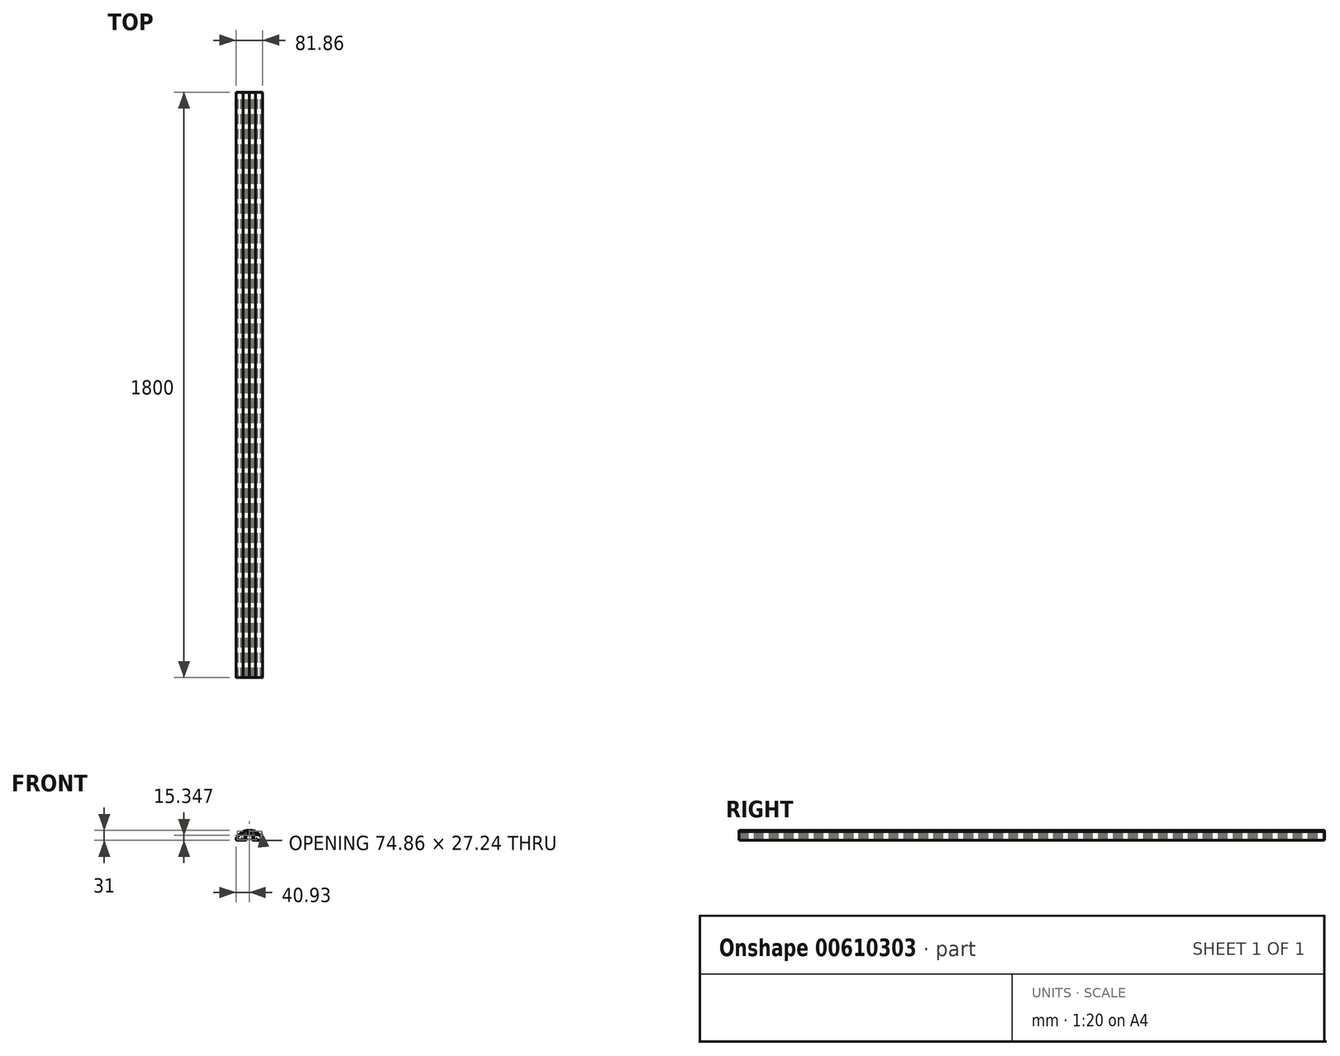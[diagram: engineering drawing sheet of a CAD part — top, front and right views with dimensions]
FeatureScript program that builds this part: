
annotation { "Feature Type Name" : "Feature", "Feature Type Description" : "" }
export const myFeature = defineFeature(function(context is Context, id is Id, definition is map)
    precondition{}
    {
        {
            var Q0;
            Q0=qCreatedBy(makeId("Front.planeOp"),FACE);
            var sketch = newSketch(context, id + "F0", { "sketchPlane" : qUnion([Q0])});
            skLineSegment(sketch, "E0.bottom", {"start": v(-41, 15.63) * mm, "end": v(41, 15.63) * mm, "construction": true});
            skLineSegment(sketch, "E0.top", {"start": v(-41, -15.37) * mm, "end": v(41, -15.37) * mm, "construction": true});
            skLineSegment(sketch, "E0.left", {"start": v(-41, 15.63) * mm, "end": v(-41, -15.37) * mm, "construction": true});
            skLineSegment(sketch, "E0.right", {"start": v(41, 15.63) * mm, "end": v(41, -15.37) * mm, "construction": true});
            skLineSegment(sketch, "E1", {"start": v(0, 15.63) * mm, "end": v(0, -15.37) * mm, "construction": true});
            skLineSegment(sketch, "E2", {"start": v(-41, 0.13) * mm, "end": v(0, 0.13) * mm, "construction": true});
            skLineSegment(sketch, "E3", {"start": v(0, 0.13) * mm, "end": v(41, 0.13) * mm, "construction": true});
            skLineSegment(sketch, "E4", {"start": v(-7.06, -1) * mm, "end": v(-6.5, 0.75) * mm});
            skLineSegment(sketch, "E5", {"start": v(-6.5, 0.75) * mm, "end": v(-8.7, 0.75) * mm});
            skLineSegment(sketch, "E6", {"start": v(-8.7, 0.75) * mm, "end": v(-8.15, 3.9) * mm});
            skLineSegment(sketch, "E7", {"start": v(-8.15, 3.9) * mm, "end": v(0, 3.9) * mm});
            skLineSegment(sketch, "E8", {"start": v(-7.06, -1) * mm, "end": v(-11.95, -1) * mm});
            skLineSegment(sketch, "E9", {"start": v(-11.95, -1) * mm, "end": v(-11.95, -5.13) * mm});
            skLineSegment(sketch, "E10", {"start": v(-11.95, -5.13) * mm, "end": v(-9.95, -5.13) * mm});
            skLineSegment(sketch, "E11", {"start": v(11.84, -5.13) * mm, "end": v(9.84, -5.13) * mm});
            skLineSegment(sketch, "E12", {"start": v(-11.8, -10.23) * mm, "end": v(-9.95, -5.13) * mm});
            skLineSegment(sketch, "E13", {"start": v(-11.8, -10.23) * mm, "end": v(-11.8, -11.67) * mm});
            skLineSegment(sketch, "E14", {"start": v(-11.8, -11.67) * mm, "end": v(-10.3, -11.67) * mm});
            skLineSegment(sketch, "E15", {"start": v(-10.3, -11.67) * mm, "end": v(-7.47, -10.23) * mm});
            skLineSegment(sketch, "E16", {"start": v(-7.47, -10.23) * mm, "end": v(-7.47, -12.86) * mm});
            skLineSegment(sketch, "E17", {"start": v(-7.47, -12.86) * mm, "end": v(-9.65, -13.96) * mm});
            skLineSegment(sketch, "E18", {"start": v(-9.65, -13.96) * mm, "end": v(-9.65, -15.37) * mm});
            skLineSegment(sketch, "E19", {"start": v(-9.65, -15.37) * mm, "end": v(-38.39, -15.37) * mm});
            skLineSegment(sketch, "E20", {"start": v(0, 5.54) * mm, "end": v(-9.18, 5.54) * mm});
            skLineSegment(sketch, "E21", {"start": v(-9.18, 5.54) * mm, "end": v(-10.28, 0.75) * mm});
            skLineSegment(sketch, "E22", {"start": v(-10.28, 0.75) * mm, "end": v(-16.43, 0.75) * mm});
            skLineSegment(sketch, "E23", {"start": v(-10.28, 0.75) * mm, "end": v(-8.7, 0.75) * mm, "construction": true});
            skLineSegment(sketch, "E24", {"start": v(-16.43, 0.75) * mm, "end": v(-16.43, -1) * mm});
            skLineSegment(sketch, "E25", {"start": v(-16.43, -1) * mm, "end": v(-13.84, -1) * mm});
            skLineSegment(sketch, "E26", {"start": v(-13.84, -1) * mm, "end": v(-13.84, -6.9) * mm});
            skLineSegment(sketch, "E27", {"start": v(-13.84, -1) * mm, "end": v(-11.95, -1) * mm, "construction": true});
            skLineSegment(sketch, "E28", {"start": v(-13.84, -6.9) * mm, "end": v(-12.94, -6.9) * mm});
            skLineSegment(sketch, "E29", {"start": v(-12.94, -6.9) * mm, "end": v(-14.57, -11.65) * mm});
            skLineSegment(sketch, "E30", {"start": v(-14.57, -11.65) * mm, "end": v(-15.13, -11.65) * mm});
            skLineSegment(sketch, "E31", {"start": v(-15.13, -11.65) * mm, "end": v(-15.13, -9.4) * mm});
            skLineSegment(sketch, "E32", {"start": v(-15.13, -9.4) * mm, "end": v(-17, -9.4) * mm});
            skLineSegment(sketch, "E33", {"start": v(-17, -9.4) * mm, "end": v(-17, -13.64) * mm});
            skLineSegment(sketch, "E34", {"start": v(-17, -13.64) * mm, "end": v(-22.16, -13.64) * mm});
            skLineSegment(sketch, "E35", {"start": v(-22.16, -13.64) * mm, "end": v(-22.16, -9.4) * mm});
            skLineSegment(sketch, "E36", {"start": v(-22.16, -9.4) * mm, "end": v(-24.46, -9.4) * mm});
            skLineSegment(sketch, "E37", {"start": v(-24.46, -9.4) * mm, "end": v(-24.46, -13.64) * mm});
            skLineSegment(sketch, "E38", {"start": v(-24.46, -13.64) * mm, "end": v(-34.73, -13.64) * mm});
            skLineSegment(sketch, "E39", {"start": v(-22.19, 7.15) * mm, "end": v(-16.85, 7.15) * mm});
            skLineSegment(sketch, "E40", {"start": v(-16.85, 7.15) * mm, "end": v(-16.85, 11.3) * mm});
            skLineSegment(sketch, "E41", {"start": v(-18.7, 11.4) * mm, "end": v(-18.7, 13.09) * mm});
            skLineSegment(sketch, "E42", {"start": v(-22.19, 1.2) * mm, "end": v(-22.19, 7.15) * mm});
            skLineSegment(sketch, "E43", {"start": v(-24.81, 5.58) * mm, "end": v(-24.81, 1.2) * mm});
            skLineSegment(sketch, "E44", {"start": v(-24.81, 1.2) * mm, "end": v(-22.19, 1.2) * mm});
            skFitSpline(sketch, "E45", {"points": [v(-18.7, 13.09) * mm, v(-15.64, 13.84) * mm, v(-13.16, 14.36) * mm, v(-10.15, 14.85) * mm, v(-6.9, 15.2) * mm, v(0, 15.63) * mm], "startDerivative": vector(17, 4.32) * mm, "endDerivative": vector(27.54, 0.89) * mm});
            skArc(sketch, "E46", {"start": v(-37.1, -8.02) * mm, "mid": v(-37.1, -11.33) * mm, "end": v(-34.73, -13.64) * mm});
            skArc(sketch, "E47", {"start": v(-40.46, -8.97) * mm, "mid": v(-40.69, -12.58) * mm, "end": v(-38.39, -15.37) * mm});
            skFitSpline(sketch, "E48", {"points": [v(-37.1, -8.02) * mm, v(-34.41, -4.02) * mm, v(-30.16, 0.77) * mm, v(-27.05, 3.65) * mm, v(-24.81, 5.58) * mm], "startDerivative": vector(8.24, 15.46) * mm, "endDerivative": vector(6.94, 5.1) * mm});
            skFitSpline(sketch, "E49", {"points": [v(-40.46, -8.97) * mm, v(-38.2, -5.17) * mm, v(-35.61, -1.81) * mm, v(-32.73, 1.25) * mm, v(-28.9, 4.9) * mm, v(-24.7, 8.14) * mm, v(-20.92, 10.33) * mm, v(-18.7, 11.4) * mm], "startDerivative": vector(14.36, 30.6) * mm, "endDerivative": vector(19.32, 6.94) * mm});
            skFitSpline(sketch, "E50", {"points": [v(-16.85, 11.3) * mm, v(-13.6, 12.07) * mm, v(-10.7, 12.63) * mm, v(-6.16, 13.17) * mm, v(-2.5, 13.5) * mm, v(0, 13.6) * mm], "startDerivative": vector(16.85, 4.06) * mm, "endDerivative": vector(13.99, 0.3) * mm});
            skFitSpline(sketch, "E51.MirrorCS", {"points": [v(16.85, 11.3) * mm, v(13.6, 12.07) * mm, v(10.7, 12.63) * mm, v(6.16, 13.17) * mm, v(2.5, 13.5) * mm, v(0, 13.6) * mm], "startDerivative": vector(-16.85, 4.06) * mm, "endDerivative": vector(-13.99, 0.3) * mm});
            skFitSpline(sketch, "E52.MirrorCS", {"points": [v(18.7, 13.09) * mm, v(15.64, 13.84) * mm, v(13.16, 14.36) * mm, v(10.15, 14.85) * mm, v(6.9, 15.2) * mm, v(0, 15.63) * mm], "startDerivative": vector(-17, 4.32) * mm, "endDerivative": vector(-27.54, 0.89) * mm});
            skLineSegment(sketch, "E53.MirrorCS", {"start": v(18.7, 11.4) * mm, "end": v(18.7, 13.09) * mm});
            skLineSegment(sketch, "E54.MirrorCS", {"start": v(16.85, 7.15) * mm, "end": v(16.85, 11.3) * mm});
            skLineSegment(sketch, "E55.MirrorCS", {"start": v(22.19, 7.15) * mm, "end": v(16.85, 7.15) * mm});
            skFitSpline(sketch, "E56.MirrorCS", {"points": [v(40.46, -8.97) * mm, v(38.2, -5.17) * mm, v(35.61, -1.81) * mm, v(32.73, 1.25) * mm, v(28.9, 4.9) * mm, v(24.7, 8.14) * mm, v(20.92, 10.33) * mm, v(18.7, 11.4) * mm], "startDerivative": vector(-14.36, 30.6) * mm, "endDerivative": vector(-19.32, 6.94) * mm});
            skLineSegment(sketch, "E57.MirrorCS", {"start": v(22.19, 1.2) * mm, "end": v(22.19, 7.15) * mm});
            skLineSegment(sketch, "E58.MirrorCS", {"start": v(24.81, 1.2) * mm, "end": v(22.19, 1.2) * mm});
            skLineSegment(sketch, "E59.MirrorCS", {"start": v(24.81, 5.58) * mm, "end": v(24.81, 1.2) * mm});
            skFitSpline(sketch, "E60.MirrorCS", {"points": [v(37.1, -8.02) * mm, v(34.41, -4.02) * mm, v(30.16, 0.77) * mm, v(27.05, 3.65) * mm, v(24.81, 5.58) * mm], "startDerivative": vector(-8.24, 15.46) * mm, "endDerivative": vector(-6.94, 5.1) * mm});
            skArc(sketch, "E61.MirrorCS", {"start": v(37.1, -8.02) * mm, "mid": v(37.1, -11.33) * mm, "end": v(34.73, -13.64) * mm});
            skArc(sketch, "E62.MirrorCS", {"start": v(40.46, -8.97) * mm, "mid": v(40.69, -12.58) * mm, "end": v(38.39, -15.37) * mm});
            skLineSegment(sketch, "E63.MirrorCS", {"start": v(24.46, -13.64) * mm, "end": v(34.73, -13.64) * mm});
            skLineSegment(sketch, "E64.MirrorCS", {"start": v(24.46, -9.4) * mm, "end": v(24.46, -13.64) * mm});
            skLineSegment(sketch, "E65.MirrorCS", {"start": v(22.16, -9.4) * mm, "end": v(24.46, -9.4) * mm});
            skLineSegment(sketch, "E66.MirrorCS", {"start": v(22.16, -13.64) * mm, "end": v(22.16, -9.4) * mm});
            skLineSegment(sketch, "E67.MirrorCS", {"start": v(17, -13.64) * mm, "end": v(22.16, -13.64) * mm});
            skLineSegment(sketch, "E68.MirrorCS", {"start": v(17, -9.4) * mm, "end": v(17, -13.64) * mm});
            skLineSegment(sketch, "E69.MirrorCS", {"start": v(15.13, -9.4) * mm, "end": v(17, -9.4) * mm});
            skLineSegment(sketch, "E70.MirrorCS", {"start": v(15.13, -11.65) * mm, "end": v(15.13, -9.4) * mm});
            skLineSegment(sketch, "E71.MirrorCS", {"start": v(14.57, -11.65) * mm, "end": v(15.13, -11.65) * mm});
            skLineSegment(sketch, "E72.MirrorCS", {"start": v(12.94, -6.9) * mm, "end": v(14.57, -11.65) * mm});
            skLineSegment(sketch, "E73.MirrorCS", {"start": v(13.84, -6.9) * mm, "end": v(12.94, -6.9) * mm});
            skLineSegment(sketch, "E74.MirrorCS", {"start": v(13.84, -1) * mm, "end": v(13.84, -6.9) * mm});
            skLineSegment(sketch, "E75.MirrorCS", {"start": v(16.43, -1) * mm, "end": v(13.84, -1) * mm});
            skLineSegment(sketch, "E76.MirrorCS", {"start": v(13.84, -1) * mm, "end": v(11.95, -1) * mm, "construction": true});
            skLineSegment(sketch, "E77.MirrorCS", {"start": v(16.43, 0.75) * mm, "end": v(16.43, -1) * mm});
            skLineSegment(sketch, "E78.MirrorCS", {"start": v(10.28, 0.75) * mm, "end": v(16.43, 0.75) * mm});
            skLineSegment(sketch, "E79.MirrorCS", {"start": v(10.28, 0.75) * mm, "end": v(8.7, 0.75) * mm, "construction": true});
            skLineSegment(sketch, "E80.MirrorCS", {"start": v(6.5, 0.75) * mm, "end": v(8.7, 0.75) * mm});
            skLineSegment(sketch, "E81.MirrorCS", {"start": v(7.06, -1) * mm, "end": v(6.5, 0.75) * mm});
            skLineSegment(sketch, "E82.MirrorCS", {"start": v(7.06, -1) * mm, "end": v(11.95, -1) * mm});
            skLineSegment(sketch, "E83.MirrorCS", {"start": v(11.95, -1) * mm, "end": v(11.95, -5.13) * mm});
            skLineSegment(sketch, "E84.MirrorCS", {"start": v(11.8, -10.23) * mm, "end": v(9.95, -5.13) * mm});
            skLineSegment(sketch, "E85.MirrorCS", {"start": v(11.8, -10.23) * mm, "end": v(11.8, -11.67) * mm});
            skLineSegment(sketch, "E86.MirrorCS", {"start": v(11.8, -11.67) * mm, "end": v(10.3, -11.67) * mm});
            skLineSegment(sketch, "E87.MirrorCS", {"start": v(8.7, 0.75) * mm, "end": v(8.15, 3.9) * mm});
            skLineSegment(sketch, "E88.MirrorCS", {"start": v(9.18, 5.54) * mm, "end": v(10.28, 0.75) * mm});
            skLineSegment(sketch, "E89.MirrorCS", {"start": v(8.15, 3.9) * mm, "end": v(0, 3.9) * mm});
            skLineSegment(sketch, "E90.MirrorCS", {"start": v(0, 5.54) * mm, "end": v(9.18, 5.54) * mm});
            skLineSegment(sketch, "E91.MirrorCS", {"start": v(10.3, -11.67) * mm, "end": v(7.47, -10.23) * mm});
            skLineSegment(sketch, "E92.MirrorCS", {"start": v(7.47, -10.23) * mm, "end": v(7.47, -12.86) * mm});
            skLineSegment(sketch, "E93.MirrorCS", {"start": v(7.47, -12.86) * mm, "end": v(9.65, -13.96) * mm});
            skLineSegment(sketch, "E94.MirrorCS", {"start": v(9.65, -13.96) * mm, "end": v(9.65, -15.37) * mm});
            skLineSegment(sketch, "E95", {"start": v(9.65, -15.37) * mm, "end": v(38.39, -15.37) * mm});
            skLineSegment(sketch, "E96", {"start": v(0, 3.9) * mm, "end": v(0, 5.54) * mm});
            skLineSegment(sketch, "E97", {"start": v(0, 13.6) * mm, "end": v(0, 15.63) * mm});
            skSolve(sketch);
        }
        {
            var Q0;
            Q0=makeQuery(id+"F0.imprint","IMPRINT",FACE,{"disambiguationData":[TD([[makeQuery(id+"F0.imprint","IMPRINT",EDGE,{"derivedFrom":sQuery(id+"F0.wireOp",EDGE,"E4")}),1.0]])]});
            extrude(context, id + "F1", {"entities" : qUnion([Q0]), "depth" : 1800 * mm, "offsetDistance" : 25 * mm});
        }
        {
            var Q0;
            Q0=makeQuery(id+"F1.opExtrude","SWEPT_BODY",BODY,{"disambiguationData":[OSD([sQuery(id+"F0.wireOp",EDGE,"E4"),sQuery(id+"F0.wireOp",EDGE,"E5"),sQuery(id+"F0.wireOp",EDGE,"E6"),sQuery(id+"F0.wireOp",EDGE,"E7"),sQuery(id+"F0.wireOp",EDGE,"E8"),sQuery(id+"F0.wireOp",EDGE,"E9"),sQuery(id+"F0.wireOp",EDGE,"E10"),sQuery(id+"F0.wireOp",EDGE,"E12"),sQuery(id+"F0.wireOp",EDGE,"E13"),sQuery(id+"F0.wireOp",EDGE,"E14"),sQuery(id+"F0.wireOp",EDGE,"E15"),sQuery(id+"F0.wireOp",EDGE,"E16"),sQuery(id+"F0.wireOp",EDGE,"E17"),sQuery(id+"F0.wireOp",EDGE,"E18"),sQuery(id+"F0.wireOp",EDGE,"E19"),sQuery(id+"F0.wireOp",EDGE,"E20"),sQuery(id+"F0.wireOp",EDGE,"E21"),sQuery(id+"F0.wireOp",EDGE,"E22"),sQuery(id+"F0.wireOp",EDGE,"E24"),sQuery(id+"F0.wireOp",EDGE,"E25"),sQuery(id+"F0.wireOp",EDGE,"E26"),sQuery(id+"F0.wireOp",EDGE,"E28"),sQuery(id+"F0.wireOp",EDGE,"E29"),sQuery(id+"F0.wireOp",EDGE,"E30"),sQuery(id+"F0.wireOp",EDGE,"E31"),sQuery(id+"F0.wireOp",EDGE,"E32"),sQuery(id+"F0.wireOp",EDGE,"E33"),sQuery(id+"F0.wireOp",EDGE,"E34"),sQuery(id+"F0.wireOp",EDGE,"E35"),sQuery(id+"F0.wireOp",EDGE,"E36"),sQuery(id+"F0.wireOp",EDGE,"E37"),sQuery(id+"F0.wireOp",EDGE,"E38"),sQuery(id+"F0.wireOp",EDGE,"E39"),sQuery(id+"F0.wireOp",EDGE,"E40"),sQuery(id+"F0.wireOp",EDGE,"E41"),sQuery(id+"F0.wireOp",EDGE,"E42"),sQuery(id+"F0.wireOp",EDGE,"E43"),sQuery(id+"F0.wireOp",EDGE,"E44"),sQuery(id+"F0.wireOp",EDGE,"E45"),sQuery(id+"F0.wireOp",EDGE,"E46"),sQuery(id+"F0.wireOp",EDGE,"E47"),sQuery(id+"F0.wireOp",EDGE,"E48"),sQuery(id+"F0.wireOp",EDGE,"E49"),sQuery(id+"F0.wireOp",EDGE,"E50"),sQuery(id+"F0.wireOp",EDGE,"E96"),sQuery(id+"F0.wireOp",EDGE,"E97")])]});
            var Q1;
            Q1=qCreatedBy(makeId("Right.planeOp"),FACE);
            mirror(context, id + "F2", {"operationType" : NewBodyOperationType.ADD, "entities" : qUnion([Q0]), "mirrorPlane" : qUnion([Q1])});
        }
    });
